FCSTD DOCUMENT  (FreeCAD 0.19R24276 (Git))
Label: Gear_no_screw
License: All rights reserved
LicenseURL: http://en.wikipedia.org/wiki/All_rights_reserved
objects: Sketcher::SketchObject×1, PartDesign::Body×1
note: 2 computed .brp shape members not serialized (recipe doc carries the construction recipe); baked Part::Feature solids carry a one-line shape summary decoded from their .brp

FEATURE [Sketcher::SketchObject] Sketch
  FullyConstrained = false
  MapMode = 5
  Support = -> [XY_Plane]
  sketch-geometry (23):
    g0: Circle CenterX=0 CenterY=0 CenterZ=0 NormalX=0 NormalY=0 NormalZ=1 AngleXU=0 Radius=4.25
    g1: Circle CenterX=15.75 CenterY=0 CenterZ=0 NormalX=0 NormalY=0 NormalZ=1 AngleXU=0 Radius=2.65
    g2: Circle CenterX=-15.75 CenterY=0 CenterZ=0 NormalX=0 NormalY=0 NormalZ=1 AngleXU=0 Radius=2.65
    g3: ArcOfCircle CenterX=15.75 CenterY=0 CenterZ=0 NormalX=0 NormalY=0 NormalZ=1 AngleXU=0 Radius=5 StartAngle=5.04775 EndAngle=7.43868
    g4: ArcOfCircle CenterX=-15.75 CenterY=0 CenterZ=0 NormalX=0 NormalY=0 NormalZ=1 AngleXU=0 Radius=5 StartAngle=1.9861 EndAngle=4.37703
    g5: LineSegment StartX=-10 StartY=14 StartZ=0 EndX=10 EndY=14 EndZ=0
    g6: LineSegment StartX=10 StartY=14 StartZ=0 EndX=10 EndY=8 EndZ=0
    g7: LineSegment StartX=-10 StartY=14 StartZ=0 EndX=-10 EndY=8 EndZ=0
    g8: LineSegment StartX=0 StartY=0 StartZ=0 EndX=0 EndY=14 EndZ=0
    g9: LineSegment StartX=-17.7673 StartY=4.57497 StartZ=0 EndX=-10 EndY=8 EndZ=0
    g10: LineSegment StartX=-15.75 StartY=0 StartZ=0 EndX=-17.7673 EndY=4.57497 EndZ=0
    g11: LineSegment StartX=17.7673 StartY=4.57497 StartZ=0 EndX=10 EndY=8 EndZ=0
    g12: LineSegment StartX=17.7673 StartY=4.57497 StartZ=0 EndX=15.75 EndY=0 EndZ=0
    g13: LineSegment StartX=0 StartY=0 StartZ=0 EndX=35.766 EndY=0 EndZ=0
    g14: LineSegment StartX=-2.25 StartY=-10 StartZ=0 EndX=2.25 EndY=-10 EndZ=0
    g15: LineSegment StartX=15.75 StartY=0 StartZ=0 EndX=17.3955 EndY=-4.72147 EndZ=0
    g16: LineSegment StartX=-15.75 StartY=0 StartZ=0 EndX=-17.3955 EndY=-4.72147 EndZ=0
    g17: LineSegment StartX=17.3955 StartY=-4.72147 StartZ=0 EndX=2.25 EndY=-10 EndZ=0
    g18: LineSegment StartX=-17.3955 StartY=-4.72147 StartZ=0 EndX=-2.25 EndY=-10 EndZ=0
    g19: LineSegment StartX=0 StartY=0 StartZ=0 EndX=0 EndY=-10 EndZ=0
    g20: LineSegment StartX=-15 StartY=14 StartZ=0 EndX=-15 EndY=5.79524 EndZ=0
    g21: LineSegment StartX=15 StartY=14 StartZ=0 EndX=15 EndY=5.79524 EndZ=0
    g22: Circle CenterX=0 CenterY=0 CenterZ=0 NormalX=0 NormalY=0 NormalZ=1 AngleXU=0 Radius=22.5
  constraints (59):
    c: Coincident(g0,g-1)
    c: PointOnObject(g1,g-1)
    c: DistanceX(g2,g1) = 31.5
    c: Symmetric(g2,g1,g-1)
    c: Diameter(g0) = 8.5
    c: Diameter(g1) = 5.3
    c: Equal(g1,g2)
    c: Coincident(g3,g1)
    c: Coincident(g4,g2)
    c: Diameter(g3) = 10
    c: Equal(g4,g3)
    c: Horizontal(g5)
    c: DistanceY(g2,g5) = 14
    c: Coincident(g6,g5)
    c: Vertical(g6)
    c: Coincident(g7,g5)
    c: Vertical(g7)
    c: DistanceY(g7,g5) = 6
    c: Equal(g7,g6)
    c: Coincident(g8,g-1)
    c: PointOnObject(g8,g-2)
    c: Symmetric(g5,g5,g8)
    c: DistanceX(g5,g5) = 20
    c: Coincident(g9,g7)
    c: Coincident(g10,g2)
    c: Coincident(g10,g9)
    c: Perpendicular(g10,g9)
    c: Coincident(g11,g6)
    c: Coincident(g12,g11)
    c: Coincident(g12,g1)
    c: Coincident(g13,g-1)
    c: PointOnObject(g13,g-1)
    c: Horizontal(g14)
    c: Coincident(g15,g1)
    c: Coincident(g16,g2)
    c: Coincident(g17,g15)
    c: Coincident(g18,g16)
    c: Perpendicular(g18,g16)
    c: Perpendicular(g17,g15)
    c: Coincident(g18,g14)
    c: Coincident(g14,g17)
    c: DistanceY(g14,g-1) = 10
    c: DistanceX(g14,g14) = 4.5
    c: Coincident(g19,g-1)
    c: PointOnObject(g19,g-2)
    c: Symmetric(g14,g14,g19)
    c: Vertical(g20)
    c: Vertical(g21)
    c: Symmetric(g20,g21,g8)
    c: Horizontal(g20,g8)
    c: DistanceX(g20,g21) = 30
    c: PointOnObject(g20,g9)
    c: PointOnObject(g21,g11)
    c: Coincident(g22,g-1)
    c: Diameter(g22) = 45
    c: Coincident(g3,g15)
    c: Tangent(g3,g11) = -1.5708
    c: Coincident(g4,g9)
    c: Coincident(g4,g16)
FEATURE [PartDesign::Body] Body
  Group = -> [Sketch]
  Origin = -> Origin
